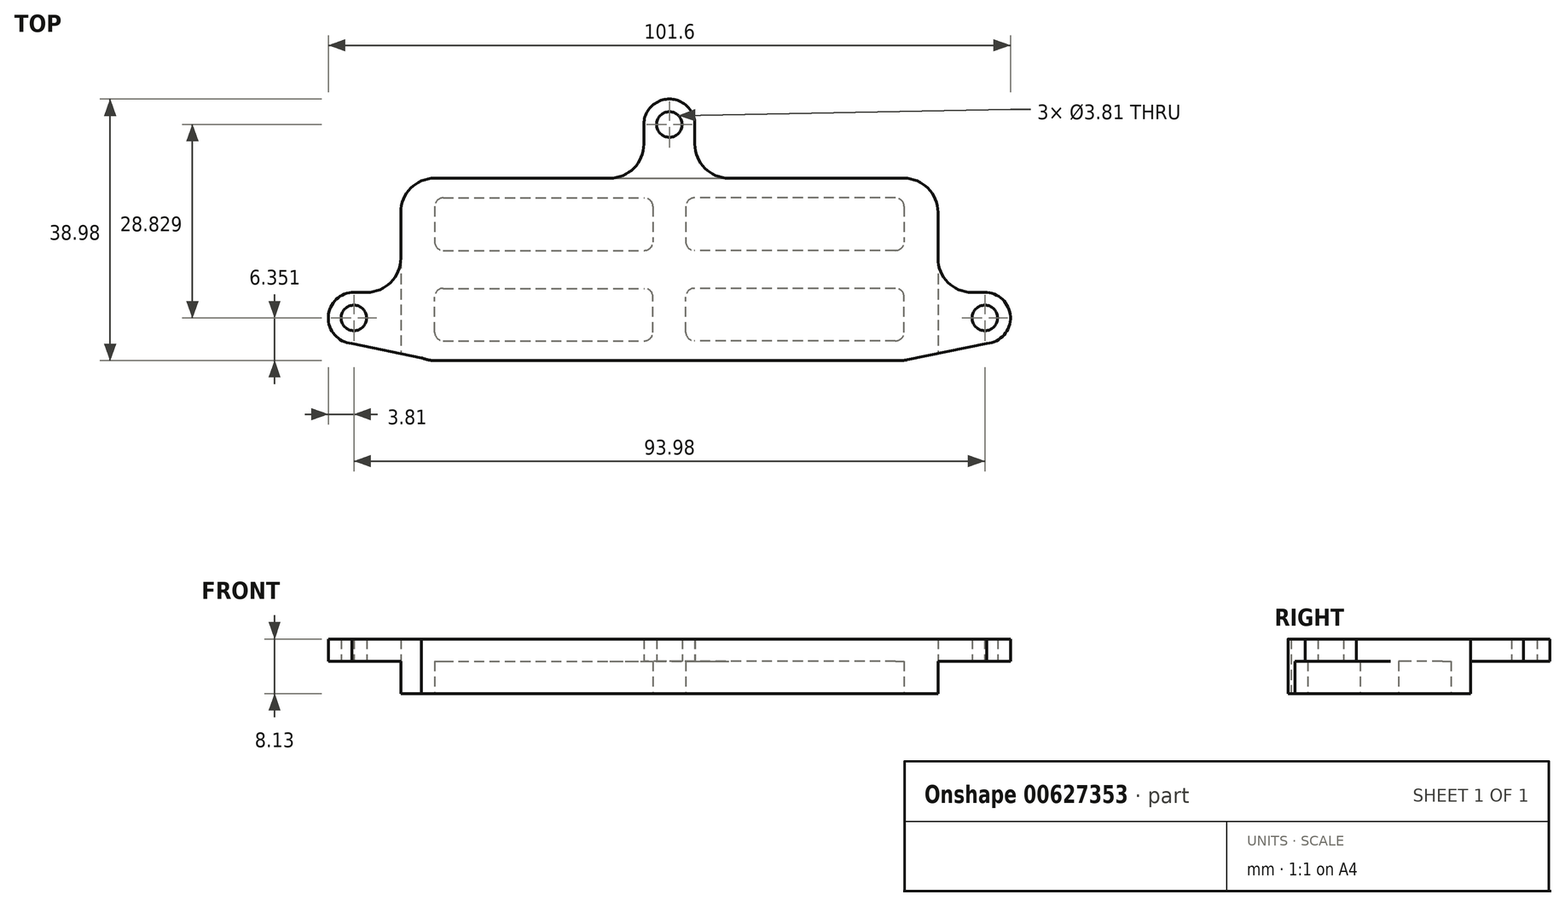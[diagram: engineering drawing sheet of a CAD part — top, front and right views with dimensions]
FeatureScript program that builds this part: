
annotation { "Feature Type Name" : "Feature", "Feature Type Description" : "" }
export const myFeature = defineFeature(function(context is Context, id is Id, definition is map)
    precondition{}
    {
        {
            var Q0;
            Q0=qCreatedBy(makeId("Top.planeOp"),FACE);
            var sketch = newSketch(context, id + "F0", { "sketchPlane" : qUnion([Q0])});
            skLineSegment(sketch, "E0.bottom", {"start": v(-34.93, 13.59) * mm, "end": v(-8.88, 13.59) * mm});
            skLineSegment(sketch, "E0.top", {"start": v(-34.93, -13.59) * mm, "end": v(34.4, -13.59) * mm});
            skLineSegment(sketch, "E0.left", {"start": v(-40, 8.5) * mm, "end": v(-40, 1.65) * mm});
            skLineSegment(sketch, "E0.right", {"start": v(40, 8.5) * mm, "end": v(40, 1.65) * mm});
            skPoint(sketch, "E0.middle", {"position": v(0, 0) * mm});
            skPoint(sketch, "E1", {"position": v(-47, -7.24) * mm});
            skPoint(sketch, "E2.MirrorP", {"position": v(47, -7.24) * mm});
            skPoint(sketch, "E3", {"position": v(0, 21.59) * mm});
            skPoint(sketch, "E4", {"position": v(-9.31, -13.59) * mm});
            skPoint(sketch, "E5.visualSharp", {"position": v(-40, 13.59) * mm});
            skArc(sketch, "E5.filletArc", {"start": v(-34.93, 13.59) * mm, "mid": v(-38.52, 12.1) * mm, "end": v(-40, 8.5) * mm});
            skArc(sketch, "E6.MirrorCS", {"start": v(-34.93, -13.59) * mm, "mid": v(-35.95, -13.48) * mm, "end": v(-36.94, -13.17) * mm});
            skArc(sketch, "E7.MirrorCS", {"start": v(34.93, 13.59) * mm, "mid": v(38.52, 12.1) * mm, "end": v(40, 8.5) * mm});
            skCircle(sketch, "E8", {"center": v(47, -7.24) * mm, "radius": 3.81 * mm});
            skCircle(sketch, "E9", {"center": v(-47, -7.24) * mm, "radius": 3.81 * mm});
            skCircle(sketch, "E10", {"center": v(0, 21.59) * mm, "radius": 3.8 * mm});
            skPoint(sketch, "E11.orphan", {"position": v(40, 13.59) * mm});
            skPoint(sketch, "E12.orphan", {"position": v(40, -13.59) * mm});
            skLineSegment(sketch, "E13", {"start": v(-3.8, 21.72) * mm, "end": v(-3.8, 18.67) * mm});
            skArc(sketch, "E14.filletArc", {"start": v(-8.88, 13.59) * mm, "mid": v(-5.29, 15.08) * mm, "end": v(-3.8, 18.67) * mm});
            skArc(sketch, "E15.MirrorCS", {"start": v(8.88, 13.59) * mm, "mid": v(5.29, 15.08) * mm, "end": v(3.8, 18.67) * mm});
            skLineSegment(sketch, "E16.MirrorCS", {"start": v(3.8, 21.72) * mm, "end": v(3.8, 18.67) * mm});
            skLineSegment(sketch, "E17", {"start": v(-47.04, -3.43) * mm, "end": v(-45.09, -3.43) * mm});
            skPoint(sketch, "E17.endSnap0", {"position": v(-40, -2.54) * mm});
            skPoint(sketch, "E18.newPointA", {"position": v(-40, -3.43) * mm});
            skPoint(sketch, "E18.newPointB", {"position": v(-40, -13.59) * mm});
            skArc(sketch, "E18.filletArc", {"start": v(-45.09, -3.43) * mm, "mid": v(-41.5, -1.94) * mm, "end": v(-40, 1.65) * mm});
            skArc(sketch, "E19.MirrorCS", {"start": v(45.09, -3.43) * mm, "mid": v(41.5, -1.94) * mm, "end": v(40, 1.65) * mm});
            skLineSegment(sketch, "E20.MirrorCS", {"start": v(47.04, -3.43) * mm, "end": v(45.09, -3.43) * mm});
            skLineSegment(sketch, "E21", {"start": v(47.3, -11.04) * mm, "end": v(35.43, -13.48) * mm});
            skPoint(sketch, "E22.orphan", {"position": v(40, -8.5) * mm});
            skPoint(sketch, "E23.visualSharp", {"position": v(34.93, -13.59) * mm});
            skArc(sketch, "E23.filletArc", {"start": v(34.4, -13.59) * mm, "mid": v(34.92, -13.56) * mm, "end": v(35.43, -13.48) * mm});
            skLineSegment(sketch, "E24.MirrorCS", {"start": v(-47.3, -11.04) * mm, "end": v(-35.43, -13.48) * mm});
            skPoint(sketch, "E25.orphan", {"position": v(-40, -8.5) * mm});
            skCircle(sketch, "E26", {"center": v(0, 21.59) * mm, "radius": 1.9 * mm});
            skCircle(sketch, "E27", {"center": v(-47, -7.24) * mm, "radius": 1.9 * mm});
            skCircle(sketch, "E28", {"center": v(47, -7.24) * mm, "radius": 1.9 * mm});
            skPoint(sketch, "E29.visualSharp", {"position": v(-34.16, 7.75) * mm});
            skPoint(sketch, "E30.orphan", {"position": v(-34.16, -7.75) * mm});
            skPoint(sketch, "E31.orphan", {"position": v(34.16, -7.75) * mm});
            skPoint(sketch, "E32.orphan", {"position": v(34.16, 7.75) * mm});
            skLineSegment(sketch, "E33", {"start": v(8.88, 13.59) * mm, "end": v(34.93, 13.59) * mm});
            skPoint(sketch, "E29.filletArc.end.orphan", {"position": v(-34.16, 5.2) * mm});
            skPoint(sketch, "E29.filletArc.start.orphan", {"position": v(-31.62, 7.75) * mm});
            skPoint(sketch, "E34.MirrorCS.end.orphan", {"position": v(-34.16, -5.2) * mm});
            skPoint(sketch, "E35.top.start.orphan", {"position": v(-31.62, -7.75) * mm});
            skPoint(sketch, "E36.MirrorCS.start.orphan", {"position": v(31.62, -7.75) * mm});
            skPoint(sketch, "E35.right.end.orphan", {"position": v(34.16, -5.2) * mm});
            skPoint(sketch, "E37.MirrorCS.end.orphan", {"position": v(34.16, 5.2) * mm});
            skPoint(sketch, "E37.MirrorCS.start.orphan", {"position": v(31.62, 7.75) * mm});
            skLineSegment(sketch, "E38", {"start": v(-40, 1.65) * mm, "end": v(-40, -12.54) * mm});
            skSolve(sketch);
        }
        {
            var Q0;
            Q0 = qSketchRegion(id + "F0", true);
            extrude(context, id + "F1", {"entities" : qUnion([Q0]), "depth" : 3.3 * mm, "offsetDistance" : 25.4 * mm});
        }
        {
            var Q0;
            Q0=makeQuery(id+"F1.opExtrude","CAP_FACE",FACE,{"disambiguationData":[OSD([sQuery(id+"F0.wireOp",EDGE,"E0.bottom"),sQuery(id+"F0.wireOp",EDGE,"E0.top"),sQuery(id+"F0.wireOp",EDGE,"E0.left"),sQuery(id+"F0.wireOp",EDGE,"E0.right"),sQuery(id+"F0.wireOp",EDGE,"E5.filletArc"),sQuery(id+"F0.wireOp",EDGE,"E6.MirrorCS"),sQuery(id+"F0.wireOp",EDGE,"E7.MirrorCS"),sQuery(id+"F0.wireOp",EDGE,"E8"),sQuery(id+"F0.wireOp",EDGE,"E9"),sQuery(id+"F0.wireOp",EDGE,"E10"),sQuery(id+"F0.wireOp",EDGE,"E13"),sQuery(id+"F0.wireOp",EDGE,"E14.filletArc"),sQuery(id+"F0.wireOp",EDGE,"E15.MirrorCS"),sQuery(id+"F0.wireOp",EDGE,"E16.MirrorCS"),sQuery(id+"F0.wireOp",EDGE,"E17"),sQuery(id+"F0.wireOp",EDGE,"E18.filletArc"),sQuery(id+"F0.wireOp",EDGE,"E19.MirrorCS"),sQuery(id+"F0.wireOp",EDGE,"E20.MirrorCS"),sQuery(id+"F0.wireOp",EDGE,"E21"),sQuery(id+"F0.wireOp",EDGE,"E23.filletArc"),sQuery(id+"F0.wireOp",EDGE,"E24.MirrorCS"),sQuery(id+"F0.wireOp",EDGE,"E26"),sQuery(id+"F0.wireOp",EDGE,"E27"),sQuery(id+"F0.wireOp",EDGE,"E28"),sQuery(id+"F0.wireOp",EDGE,"E33")])],"isStart":true});
            var sketch = newSketch(context, id + "F2", { "sketchPlane" : qUnion([Q0])});
            skLineSegment(sketch, "E39", {"start": v(-40, -5.08) * mm, "end": v(-40, 12.54) * mm});
            skLineSegment(sketch, "E40.MirrorCS", {"start": v(40, -5.08) * mm, "end": v(40, 12.54) * mm});
            skLineSegment(sketch, "E41", {"start": v(-13.13, -13.59) * mm, "end": v(9.64, -13.59) * mm});
            skSolve(sketch);
        }
        {
            var Q0;
            Q0 = qSketchRegion(id + "F2", true);
            var Q1;
            Q1=makeQuery(id+"F2.imprint","IMPRINT",FACE,{"disambiguationData":[TD([[makeQuery(id+"F2.imprint","IMPRINT",EDGE,{"derivedFrom":makeQuery(id+"F1.opExtrude","CAP_EDGE",EDGE,{"disambiguationData":[OSD([sQuery(id+"F0.wireOp",EDGE,"E0.top")])],"isStart":true})}),-1.0]])]});
            extrude(context, id + "F3", {"entities" : qUnion([Q0, Q1]), "operationType" : NewBodyOperationType.ADD, "depth" : 4.83 * mm, "offsetDistance" : 25.4 * mm});
        }
        {
            var Q0;
            Q0=makeQuery(id+"F3.opExtrude","CAP_FACE",FACE,{"disambiguationData":[OSD([sQuery(id+"F0.wireOp",EDGE,"E0.bottom"),sQuery(id+"F0.wireOp",EDGE,"E0.top"),sQuery(id+"F0.wireOp",EDGE,"E0.right"),sQuery(id+"F0.wireOp",EDGE,"E5.filletArc"),sQuery(id+"F0.wireOp",EDGE,"E6.MirrorCS"),sQuery(id+"F0.wireOp",EDGE,"E7.MirrorCS"),sQuery(id+"F0.wireOp",EDGE,"E21"),sQuery(id+"F0.wireOp",EDGE,"E23.filletArc"),sQuery(id+"F0.wireOp",EDGE,"E24.MirrorCS"),sQuery(id+"F2.wireOp",EDGE,"E39"),sQuery(id+"F2.wireOp",EDGE,"E40.MirrorCS"),sQuery(id+"F2.wireOp",EDGE,"E41")])],"isStart":false});
            var sketch = newSketch(context, id + "F4", { "sketchPlane" : qUnion([Q0])});
            skLineSegment(sketch, "E42.MirrorCS", {"start": v(-33.69, -2.83) * mm, "end": v(-3.72, -2.83) * mm});
            skLineSegment(sketch, "E43.MirrorCS", {"start": v(-2.45, -9.38) * mm, "end": v(-2.45, -4.1) * mm});
            skLineSegment(sketch, "E44.MirrorCS", {"start": v(-33.69, -10.65) * mm, "end": v(-3.72, -10.65) * mm});
            skLineSegment(sketch, "E45.MirrorCS", {"start": v(-34.96, -9.38) * mm, "end": v(-34.96, -4.1) * mm});
            skPoint(sketch, "E46.visualSharp", {"position": v(-34.96, -2.83) * mm});
            skArc(sketch, "E46.filletArc", {"start": v(-33.69, -2.83) * mm, "mid": v(-34.58, -3.2) * mm, "end": v(-34.96, -4.1) * mm});
            skPoint(sketch, "E47.visualSharp", {"position": v(-2.45, -2.83) * mm});
            skArc(sketch, "E47.filletArc", {"start": v(-2.45, -4.1) * mm, "mid": v(-2.82, -3.2) * mm, "end": v(-3.72, -2.83) * mm});
            skPoint(sketch, "E48.visualSharp", {"position": v(-2.45, -10.65) * mm});
            skArc(sketch, "E48.filletArc", {"start": v(-3.72, -10.65) * mm, "mid": v(-2.82, -10.27) * mm, "end": v(-2.45, -9.38) * mm});
            skPoint(sketch, "E49.visualSharp", {"position": v(-34.96, -10.65) * mm});
            skArc(sketch, "E49.filletArc", {"start": v(-34.96, -9.38) * mm, "mid": v(-34.58, -10.27) * mm, "end": v(-33.69, -10.65) * mm});
            skLineSegment(sketch, "E50.MirrorCS", {"start": v(2.45, -9.38) * mm, "end": v(2.45, -4.1) * mm});
            skArc(sketch, "E51.MirrorCS", {"start": v(2.45, -4.1) * mm, "mid": v(2.82, -3.2) * mm, "end": v(3.72, -2.83) * mm});
            skArc(sketch, "E52.MirrorCS", {"start": v(3.72, -10.65) * mm, "mid": v(2.82, -10.27) * mm, "end": v(2.45, -9.38) * mm});
            skLineSegment(sketch, "E53.MirrorCS", {"start": v(33.69, -10.65) * mm, "end": v(3.72, -10.65) * mm});
            skArc(sketch, "E54.MirrorCS", {"start": v(34.96, -9.38) * mm, "mid": v(34.58, -10.27) * mm, "end": v(33.69, -10.65) * mm});
            skLineSegment(sketch, "E55.MirrorCS", {"start": v(34.96, -9.38) * mm, "end": v(34.96, -4.1) * mm});
            skArc(sketch, "E56.MirrorCS", {"start": v(33.69, -2.83) * mm, "mid": v(34.58, -3.2) * mm, "end": v(34.96, -4.1) * mm});
            skLineSegment(sketch, "E57.MirrorCS", {"start": v(33.69, -2.83) * mm, "end": v(3.72, -2.83) * mm});
            skLineSegment(sketch, "E58.MirrorCS", {"start": v(-33.69, 2.83) * mm, "end": v(-3.72, 2.83) * mm});
            skArc(sketch, "E59.MirrorCS", {"start": v(-2.45, 4.1) * mm, "mid": v(-2.82, 3.2) * mm, "end": v(-3.72, 2.83) * mm});
            skLineSegment(sketch, "E60.MirrorCS", {"start": v(-2.45, 9.38) * mm, "end": v(-2.45, 4.1) * mm});
            skArc(sketch, "E61.MirrorCS", {"start": v(-3.72, 10.65) * mm, "mid": v(-2.82, 10.27) * mm, "end": v(-2.45, 9.38) * mm});
            skLineSegment(sketch, "E62.MirrorCS", {"start": v(-33.69, 10.65) * mm, "end": v(-3.72, 10.65) * mm});
            skArc(sketch, "E63.MirrorCS", {"start": v(-34.96, 9.38) * mm, "mid": v(-34.58, 10.27) * mm, "end": v(-33.69, 10.65) * mm});
            skLineSegment(sketch, "E64.MirrorCS", {"start": v(-34.96, 9.38) * mm, "end": v(-34.96, 4.1) * mm});
            skArc(sketch, "E65.MirrorCS", {"start": v(-33.69, 2.83) * mm, "mid": v(-34.58, 3.2) * mm, "end": v(-34.96, 4.1) * mm});
            skLineSegment(sketch, "E66.MirrorCS", {"start": v(2.45, 9.38) * mm, "end": v(2.45, 4.1) * mm});
            skArc(sketch, "E67.MirrorCS", {"start": v(3.72, 10.65) * mm, "mid": v(2.82, 10.27) * mm, "end": v(2.45, 9.38) * mm});
            skLineSegment(sketch, "E68.MirrorCS", {"start": v(33.69, 10.65) * mm, "end": v(3.72, 10.65) * mm});
            skArc(sketch, "E69.MirrorCS", {"start": v(34.96, 9.38) * mm, "mid": v(34.58, 10.27) * mm, "end": v(33.69, 10.65) * mm});
            skLineSegment(sketch, "E70.MirrorCS", {"start": v(34.96, 9.38) * mm, "end": v(34.96, 4.1) * mm});
            skArc(sketch, "E71.MirrorCS", {"start": v(33.69, 2.83) * mm, "mid": v(34.58, 3.2) * mm, "end": v(34.96, 4.1) * mm});
            skLineSegment(sketch, "E72.MirrorCS", {"start": v(33.69, 2.83) * mm, "end": v(3.72, 2.83) * mm});
            skArc(sketch, "E73.MirrorCS", {"start": v(2.45, 4.1) * mm, "mid": v(2.82, 3.2) * mm, "end": v(3.72, 2.83) * mm});
            skSolve(sketch);
        }
        {
            var Q0;
            Q0=makeQuery(id+"F4.imprint","IMPRINT",FACE,{"disambiguationData":[TD([[makeQuery(id+"F4.imprint","IMPRINT",EDGE,{"derivedFrom":sQuery(id+"F4.wireOp",EDGE,"E58.MirrorCS")}),1.0]])]});
            var Q1;
            Q1=makeQuery(id+"F4.imprint","IMPRINT",FACE,{"disambiguationData":[TD([[makeQuery(id+"F4.imprint","IMPRINT",EDGE,{"derivedFrom":sQuery(id+"F4.wireOp",EDGE,"E66.MirrorCS")}),1.0]])]});
            var Q2;
            Q2=makeQuery(id+"F4.imprint","IMPRINT",FACE,{"disambiguationData":[TD([[makeQuery(id+"F4.imprint","IMPRINT",EDGE,{"derivedFrom":sQuery(id+"F4.wireOp",EDGE,"E42.MirrorCS")}),-1.0]])]});
            var Q3;
            Q3=makeQuery(id+"F4.imprint","IMPRINT",FACE,{"disambiguationData":[TD([[makeQuery(id+"F4.imprint","IMPRINT",EDGE,{"derivedFrom":sQuery(id+"F4.wireOp",EDGE,"E50.MirrorCS")}),-1.0]])]});
            extrude(context, id + "F5", {"entities" : qUnion([Q0, Q1, Q2, Q3]), "operationType" : NewBodyOperationType.REMOVE, "oppositeDirection" : true, "depth" : 4.83 * mm, "offsetDistance" : 25.4 * mm});
        }
    });
